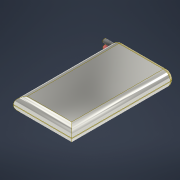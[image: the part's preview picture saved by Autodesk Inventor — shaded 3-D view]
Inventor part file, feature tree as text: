
AUTODESK INVENTOR PART (.ipt)
format: ipt  version: 2022 (Build 260153000, 153)  size: 153,088 bytes
history: native  units: in
note: dims shown in document units (in); Inventor stores cm internally (conversion verified against a paired STEP export)
features: extrude x2, fillet x2, sketch x2
ambient origin geometry x8: Origin, YZ Plane, XZ Plane, XY Plane, X Axis, Y Axis, Z Axis, Center Point
bodies: Solid1 (feature_tree)
feature tree (6):
  extrude  "Extrusion1"  Depth=0.12in
  fillet  "Fillet1"  Radius=0.25in
  fillet  "Fillet2"  Radius=0.12in
  extrude  "Extrusion2"  Depth=0.0625in
  sketch  "Sketch1"  dims[d0=1.0in d1=1.75in d2=0.25in d3=0.0in d4=0.12in]
  sketch  "Sketch2"  dims[d5=0.0625in d6=0.0625in d7=0.25in d8=0.0in]
